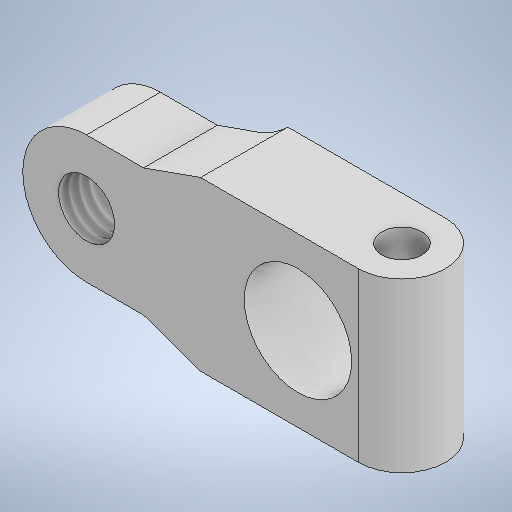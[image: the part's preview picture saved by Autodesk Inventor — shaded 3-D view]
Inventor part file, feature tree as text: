
AUTODESK INVENTOR PART (.ipt)
format: ipt  version: 2025.1 (Build 291241000, 241)  size: 261,120 bytes
history: native  units: mm
features: sketch x4, extrude x3, fillet x2, hole x2
ambient origin geometry x8: Origin, YZ Plane, XZ Plane, XY Plane, X Axis, Y Axis, Z Axis, Center Point
bodies: Volumenkörper2 (feature_tree)
feature tree (11):
  sketch  "Skizze1"  dims[d0=90.0deg d1=25.0mm]
  extrude  "Extrusion2"  Depth=25.0mm
  extrude  "Extrusion3"  Depth=47.0mm
  fillet  "Rundung1"  Radius=8.5mm
  fillet  "Rundung2"  Radius=18.0mm
  hole  "Bohrung1"  [1 undecoded]
  hole  "Bohrung2"  [1 undecoded]
  extrude  "Extrusion4"  Depth=10.0mm
  sketch  "Skizze2"  dims[d2=30.0mm d3=47.0mm d5=8.5mm d6=18.0mm]
  sketch  "Skizze3"  dims[d9=30.0mm d10=13.0mm d11=0.0mm]
  sketch  "Sketch4"  dims[d12=11.0mm d13=0.0mm d14=2.0mm d15=6.5mm d16=6.0mm d17=12.0mm d18=4.0mm d19=2.0mm d20=90.0deg d21=8.0mm d22=0.0mm d23=8.376mm d24=20.0mm d25=4.0mm d26=2.0mm d27=90.0deg d28=8.0mm d29=0.0mm d30=16.0mm d31=10.0mm d32=0.0mm d33=9.0mm]
note: 2 required parameter values undecoded (feature->parameter linkage not recoverable at this tier; creation-order binding heuristic only, values carry confidence <= 0.55)
